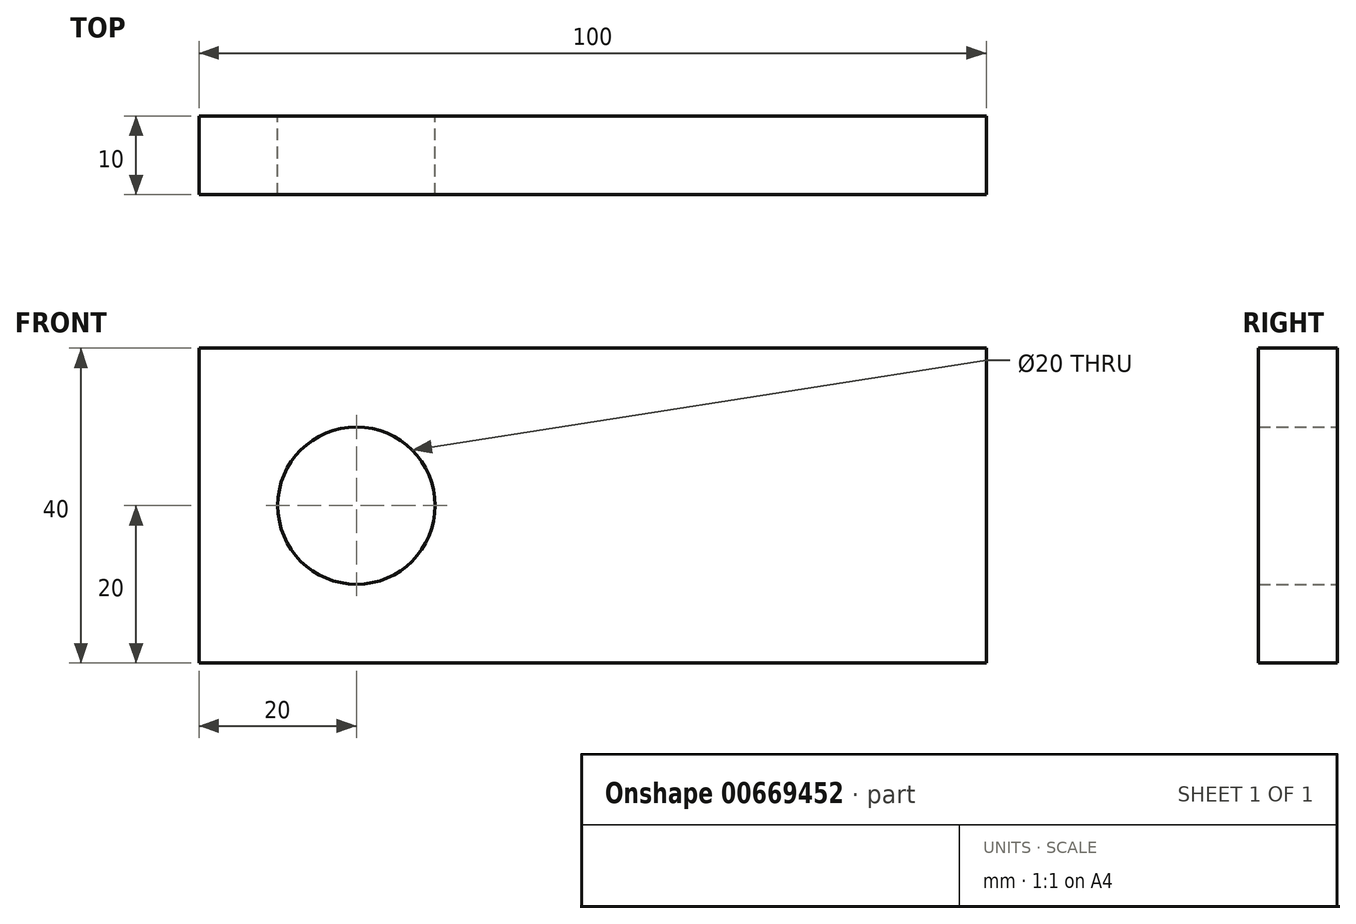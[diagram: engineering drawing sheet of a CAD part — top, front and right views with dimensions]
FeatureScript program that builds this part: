
annotation { "Feature Type Name" : "Feature", "Feature Type Description" : "" }
export const myFeature = defineFeature(function(context is Context, id is Id, definition is map)
    precondition{}
    {
        {
            var Q0;
            Q0=qCreatedBy(makeId("Front.planeOp"),FACE);
            var sketch = newSketch(context, id + "F0", { "sketchPlane" : qUnion([Q0])});
            skLineSegment(sketch, "E0.bottom", {"start": v(0, 0) * mm, "end": v(100, 0) * mm});
            skLineSegment(sketch, "E0.top", {"start": v(0, 40) * mm, "end": v(100, 40) * mm});
            skLineSegment(sketch, "E0.left", {"start": v(0, 0) * mm, "end": v(0, 40) * mm});
            skLineSegment(sketch, "E0.right", {"start": v(100, 0) * mm, "end": v(100, 40) * mm});
            skCircle(sketch, "E1", {"center": v(20, 20) * mm, "radius": 10 * mm});
            skSolve(sketch);
        }
        {
            var Q0;
            Q0=makeQuery(id+"F0.imprint","IMPRINT",FACE,{"disambiguationData":[TD([[makeQuery(id+"F0.imprint","IMPRINT",EDGE,{"derivedFrom":sQuery(id+"F0.wireOp",EDGE,"E0.bottom")}),1.0]])]});
            extrude(context, id + "F1", {"entities" : qUnion([Q0]), "depth" : 10 * mm, "offsetDistance" : 25 * mm});
        }
    });
